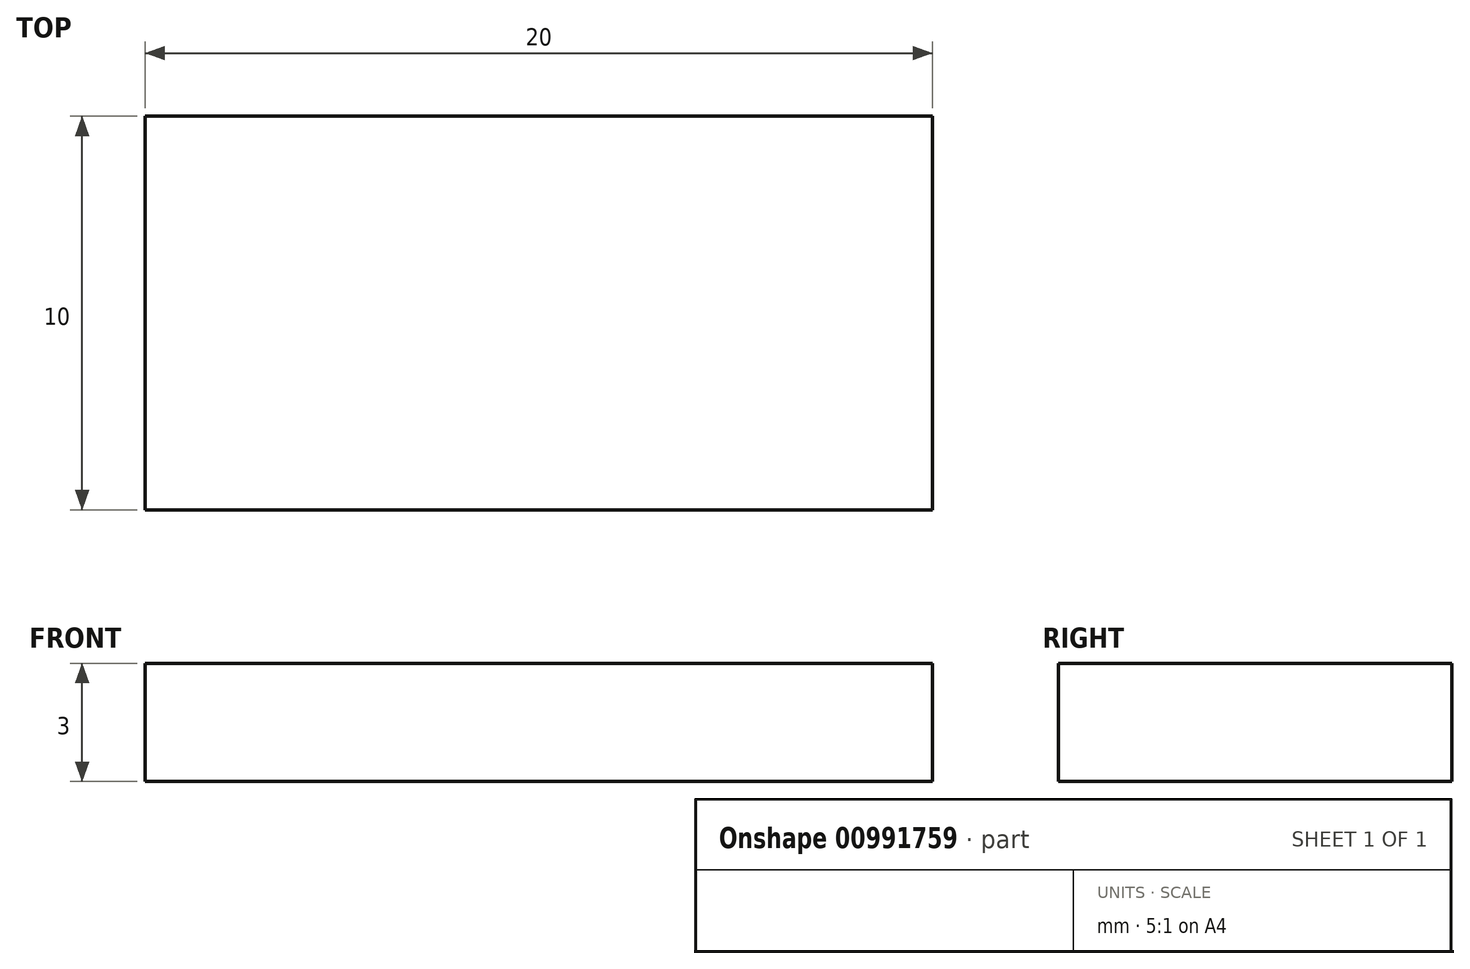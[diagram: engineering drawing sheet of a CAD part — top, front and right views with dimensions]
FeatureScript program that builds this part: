
annotation { "Feature Type Name" : "Feature", "Feature Type Description" : "" }
export const myFeature = defineFeature(function(context is Context, id is Id, definition is map)
    precondition{}
    {
        {
            var Q0;
            Q0=qCreatedBy(makeId("Top.planeOp"),FACE);
            var sketch = newSketch(context, id + "F0", { "sketchPlane" : qUnion([Q0])});
            skLineSegment(sketch, "E0.bottom", {"start": v(-10, 5) * mm, "end": v(10, 5) * mm});
            skLineSegment(sketch, "E0.top", {"start": v(-10, -5) * mm, "end": v(10, -5) * mm});
            skLineSegment(sketch, "E0.left", {"start": v(-10, 5) * mm, "end": v(-10, -5) * mm});
            skLineSegment(sketch, "E0.right", {"start": v(10, 5) * mm, "end": v(10, -5) * mm});
            skPoint(sketch, "E0.middle", {"position": v(0, 0) * mm});
            skSolve(sketch);
        }
        {
            var Q0;
            Q0 = qSketchRegion(id + "F0", true);
            extrude(context, id + "F1", {"entities" : qUnion([Q0]), "depth" : 3 * mm, "offsetDistance" : 25 * mm});
        }
    });
